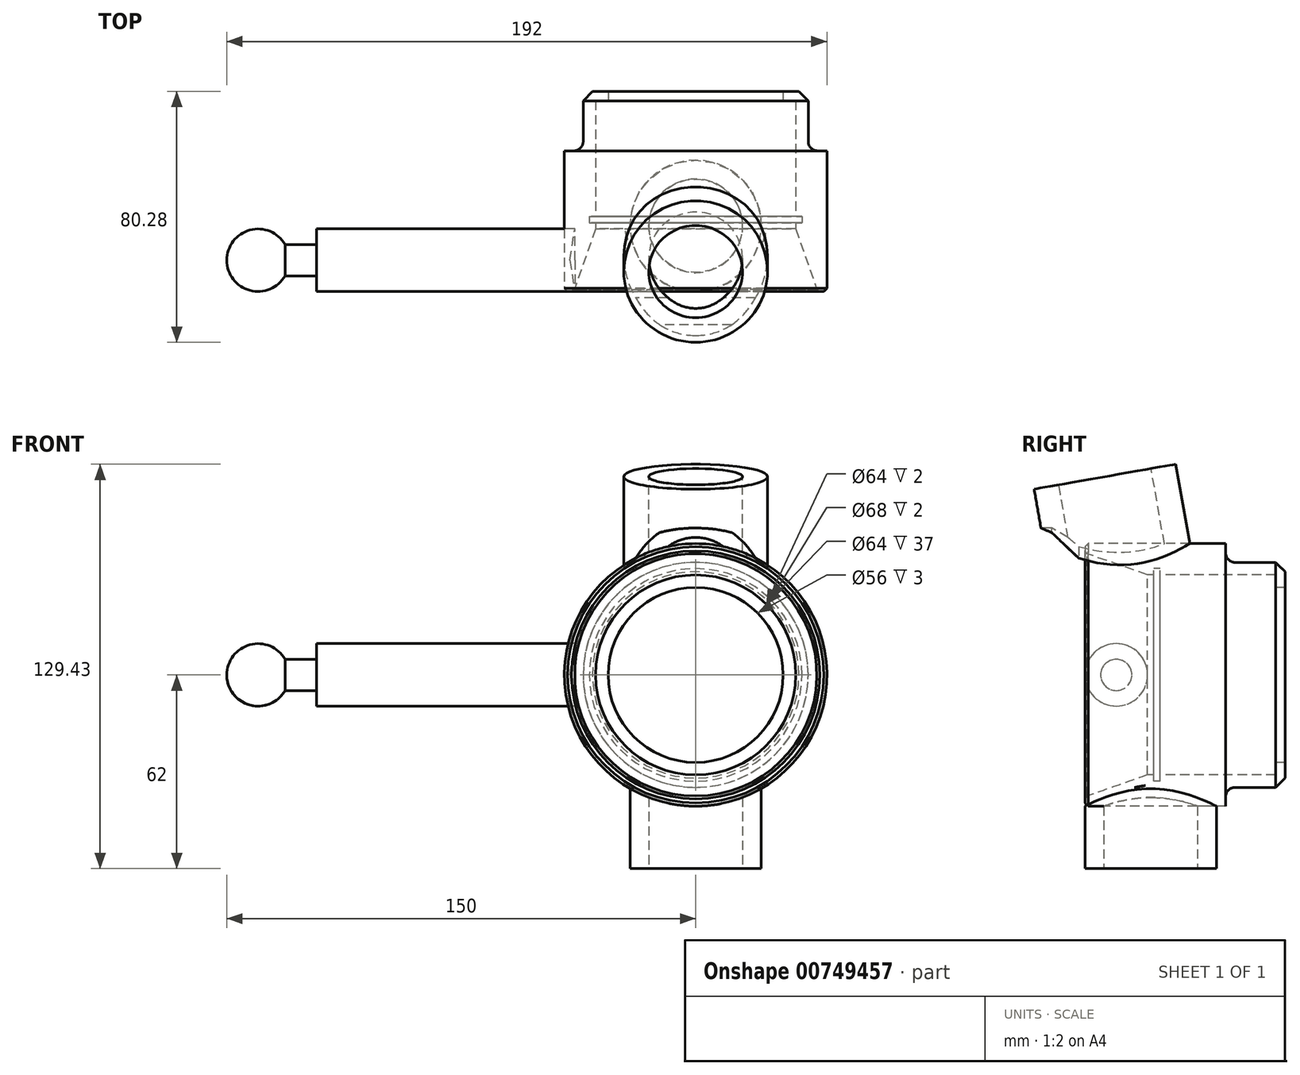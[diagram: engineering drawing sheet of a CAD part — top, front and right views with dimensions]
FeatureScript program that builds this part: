
annotation { "Feature Type Name" : "Feature", "Feature Type Description" : "" }
export const myFeature = defineFeature(function(context is Context, id is Id, definition is map)
    precondition{}
    {
        {
            var Q0;
            Q0=qCreatedBy(makeId("Right.planeOp"),FACE);
            var sketch = newSketch(context, id + "F0", { "sketchPlane" : qUnion([Q0])});
            skLineSegment(sketch, "E0", {"start": v(0, 42) * mm, "end": v(45, 42) * mm});
            skLineSegment(sketch, "E1", {"start": v(64, 36) * mm, "end": v(64, 28) * mm});
            skLineSegment(sketch, "E2", {"start": v(64, 28) * mm, "end": v(61, 28) * mm});
            skLineSegment(sketch, "E3", {"start": v(61, 28) * mm, "end": v(61, 32) * mm});
            skLineSegment(sketch, "E4", {"start": v(61, 32) * mm, "end": v(24, 32) * mm});
            skLineSegment(sketch, "E5", {"start": v(24, 32) * mm, "end": v(24, 34) * mm});
            skLineSegment(sketch, "E6", {"start": v(24, 34) * mm, "end": v(22, 34) * mm});
            skLineSegment(sketch, "E7", {"start": v(22, 34) * mm, "end": v(22, 32) * mm});
            skLineSegment(sketch, "E8", {"start": v(22, 32) * mm, "end": v(20, 32) * mm});
            skLineSegment(sketch, "E9", {"start": v(0, 39) * mm, "end": v(0, 42) * mm});
            skLineSegment(sketch, "E10", {"start": v(0, 0) * mm, "end": v(42.35, 0) * mm, "construction": true});
            skLineSegment(sketch, "E11", {"start": v(64, 36) * mm, "end": v(48, 36) * mm});
            skLineSegment(sketch, "E12", {"start": v(45, 39) * mm, "end": v(45, 42) * mm});
            skPoint(sketch, "E13.orphan", {"position": v(0, 32) * mm});
            skPoint(sketch, "E14.visualSharp", {"position": v(45, 36) * mm});
            skArc(sketch, "E14.filletArc", {"start": v(45, 39) * mm, "mid": v(45.88, 36.88) * mm, "end": v(48, 36) * mm});
            skPoint(sketch, "E15.visualSharp", {"position": v(19, 39) * mm});
            skLineSegment(sketch, "E16", {"start": v(0, 39) * mm, "end": v(20, 32) * mm});
            skSolve(sketch);
        }
        {
            var Q0;
            Q0 = qSketchRegion(id + "F0", true);
            var Q1;
            Q1=sQuery(id+"F0.wireOp",EDGE,"E10");
            revolve(context, id + "F1", {"surfaceOperationType" : NewSurfaceOperationType.NEW, "entities" : qUnion([Q0]), "axis" : qUnion([Q1]), "revolveType" : RevolveType.FULL});
        }
        {
            var Q0;
            Q0=qCreatedBy(makeId("Top.planeOp"),FACE);
            cPlane(context, id + "F2", {"entities" : qUnion([Q0]), "cplaneType" : CPlaneType.OFFSET, "offset" : (64 / 2 + 10) * mm, "oppositeDirection" : true, "width" : 150 * mm, "height" : 150 * mm});
        }
        {
            var Q0;
            Q0=qCreatedBy(id+"F2.planeOp",FACE);
            var sketch = newSketch(context, id + "F3", { "sketchPlane" : qUnion([Q0])});
            skCircle(sketch, "E17", {"center": v(0, 21) * mm, "radius": 21 * mm});
            skCircle(sketch, "E18", {"center": v(0, 21) * mm, "radius": 15 * mm});
            skSolve(sketch);
        }
        {
            var Q0;
            Q0 = qSketchRegion(id + "F3", true);
            extrude(context, id + "F4", {"entities" : qUnion([Q0]), "endBound" : BoundingType.UP_TO_NEXT, "depth" : 25 * mm, "offsetDistance" : 25 * mm, "hasSecondDirection" : true, "secondDirectionOppositeDirection" : true, "secondDirectionDepth" : 20 * mm});
        }
        {
            var Q0;
            Q0=qCreatedBy(makeId("Top.planeOp"),FACE);
            cPlane(context, id + "F5", {"entities" : qUnion([Q0]), "cplaneType" : CPlaneType.OFFSET, "offset" : (64 / 2 + 10) * mm, "width" : 150 * mm, "height" : 150 * mm});
        }
        {
            var Q0;
            Q0=qCreatedBy(id+"F5.planeOp",FACE);
            var sketch = newSketch(context, id + "F6", { "sketchPlane" : qUnion([Q0])});
            skLineSegment(sketch, "E19.0.0", {"start": v(42, 0) * mm, "end": v(-42, 0) * mm, "construction": true});
            skSolve(sketch);
        }
        {
            var Q0;
            Q0=sQuery(id+"F6.wireOp",EDGE,"E19.0.0");
            cPlane(context, id + "F7", {"entities" : qUnion([Q0]), "cplaneType" : CPlaneType.LINE_ANGLE, "offset" : 25 * mm, "angle" : 80 * degree, "width" : 150 * mm, "height" : 150 * mm});
        }
        {
            var Q0;
            Q0=qCreatedBy(id+"F7.planeOp",FACE);
            var sketch = newSketch(context, id + "F8", { "sketchPlane" : qUnion([Q0])});
            skCircle(sketch, "E20", {"center": v(0, 17.3) * mm, "radius": 23 * mm});
            skCircle(sketch, "E21", {"center": v(0, 17.3) * mm, "radius": 15 * mm});
            skSolve(sketch);
        }
        {
            var Q0;
            Q0=makeQuery(id+"F8.imprint","IMPRINT",FACE,{"disambiguationData":[TD([[makeQuery(id+"F8.imprint","IMPRINT",EDGE,{"derivedFrom":sQuery(id+"F8.wireOp",EDGE,"E20")}),1.0]])]});
            extrude(context, id + "F9", {"entities" : qUnion([Q0]), "oppositeDirection" : true, "depth" : 79.6 * mm, "offsetDistance" : 25 * mm, "hasSecondDirection" : true, "secondDirectionOppositeDirection" : false, "secondDirectionDepth" : 20 * mm});
        }
        {
            var Q0;
            Q0=qCreatedBy(makeId("Right.planeOp"),FACE);
            var sketch = newSketch(context, id + "F10", { "sketchPlane" : qUnion([Q0])});
            skLineSegment(sketch, "E22", {"start": v(45, 42) * mm, "end": v(-2, 42) * mm});
            skLineSegment(sketch, "E23", {"start": v(75.04, 0) * mm, "end": v(-49, 0) * mm});
            skLineSegment(sketch, "E24", {"start": v(-49, 0) * mm, "end": v(75.04, 0) * mm});
            skLineSegment(sketch, "E25", {"start": v(-49, 42) * mm, "end": v(-49, 0) * mm});
            skLineSegment(sketch, "E26.bottom", {"start": v(75.04, 42) * mm, "end": v(75.08, 42) * mm});
            skLineSegment(sketch, "E26.top", {"start": v(45, 62) * mm, "end": v(75.08, 62) * mm});
            skLineSegment(sketch, "E26.left", {"start": v(45, 42) * mm, "end": v(45, 62) * mm});
            skLineSegment(sketch, "E27", {"start": v(-2, 42) * mm, "end": v(-10.66, 47) * mm});
            skLineSegment(sketch, "E28", {"start": v(-10.66, 47) * mm, "end": v(-49, 47) * mm});
            skLineSegment(sketch, "E29", {"start": v(-49, 47) * mm, "end": v(-49, 42) * mm});
            skLineSegment(sketch, "E30", {"start": v(75.08, 62) * mm, "end": v(75.04, 0) * mm});
            skSolve(sketch);
        }
        {
            var Q0;
            Q0=makeQuery(id+"F10.imprint","IMPRINT",FACE,{"disambiguationData":[TD([[makeQuery(id+"F10.imprint","IMPRINT",EDGE,{"derivedFrom":sQuery(id+"F10.wireOp",EDGE,"E22")}),1.0]])]});
            var Q1;
            Q1=sQuery(id+"F10.wireOp",EDGE,"E24");
            revolve(context, id + "F11", {"surfaceOperationType" : NewSurfaceOperationType.NEW, "entities" : qUnion([Q0]), "axis" : qUnion([Q1]), "revolveType" : RevolveType.FULL});
        }
        {
            var Q0;
            Q0=makeQuery(id+"F1.opRevolve","SWEPT_EDGE",EDGE,{"disambiguationData":[OSD([sQuery(id+"F0.wireOp",EDGE,"E1"),sQuery(id+"F0.wireOp",EDGE,"E11")])]});
            chamfer(context, id + "F12", {"entities" : qUnion([Q0]), "width" : 3 * mm, "tangentPropagation" : true});
        }
        {
            var Q0;
            Q0=makeQuery(id+"F1.opRevolve","SWEPT_EDGE",EDGE,{"disambiguationData":[OSD([sQuery(id+"F0.wireOp",EDGE,"E9"),sQuery(id+"F0.wireOp",EDGE,"IUdjLPdn-Iqcu-OCA8-yRft-X54qKW0S89eC")])]});
            chamfer(context, id + "F13", {"entities" : qUnion([Q0]), "width" : 1 * mm, "tangentPropagation" : true});
        }
        {
            var Q0;
            Q0=makeQuery(id+"F11.opRevolve","SWEPT_BODY",BODY,{"disambiguationData":[OSD([sQuery(id+"F10.wireOp",EDGE,"E22"),sQuery(id+"F10.wireOp",EDGE,"E24"),sQuery(id+"F10.wireOp",EDGE,"E25"),sQuery(id+"F10.wireOp",EDGE,"E26.top"),sQuery(id+"F10.wireOp",EDGE,"E26.left"),sQuery(id+"F10.wireOp",EDGE,"E27"),sQuery(id+"F10.wireOp",EDGE,"E28"),sQuery(id+"F10.wireOp",EDGE,"E29"),sQuery(id+"F10.wireOp",EDGE,"E30")])]});
            var Q1;
            Q1=makeQuery(id+"F9.opExtrude","SWEPT_BODY",BODY,{"disambiguationData":[OSD([sQuery(id+"F8.wireOp",EDGE,"E20"),sQuery(id+"F8.wireOp",EDGE,"E21")])]});
            booleanBodies(context, id + "F14", {"operationType" : BooleanOperationType.SUBTRACTION, "tools" : qUnion([Q0]), "targets" : qUnion([Q1])});
        }
        {
            var Q0;
            Q0=makeQuery(id+"F1.opRevolve","SWEPT_FACE",FACE,{"disambiguationData":[OSD([sQuery(id+"F0.wireOp",EDGE,"E12")])]});
            cPlane(context, id + "F15", {"entities" : qUnion([Q0]), "cplaneType" : CPlaneType.OFFSET, "offset" : 35 * mm, "oppositeDirection" : true, "width" : 150 * mm, "height" : 150 * mm});
        }
        {
            var Q0;
            Q0=qCreatedBy(id+"F15.planeOp",FACE);
            var sketch = newSketch(context, id + "F16", { "sketchPlane" : qUnion([Q0])});
            skLineSegment(sketch, "E31", {"start": v(38.67, 10) * mm, "end": v(121.34, 10) * mm});
            skLineSegment(sketch, "E32", {"start": v(121.34, 10) * mm, "end": v(121.34, 5) * mm});
            skLineSegment(sketch, "E33", {"start": v(121.34, 5) * mm, "end": v(131.34, 5) * mm});
            skLineSegment(sketch, "E34", {"start": v(150, 0) * mm, "end": v(40.25, 0) * mm});
            skArc(sketch, "E35", {"start": v(131.34, 5) * mm, "mid": v(142.59, 9.66) * mm, "end": v(150, 0) * mm});
            skPoint(sketch, "E36.orphan", {"position": v(49.78, 10) * mm});
            skPoint(sketch, "E37.orphan", {"position": v(49.78, 0) * mm});
            skLineSegment(sketch, "E38", {"start": v(38.67, 10) * mm, "end": v(40.25, 0) * mm});
            skSolve(sketch);
        }
        {
            var Q0;
            Q0 = qSketchRegion(id + "F16", true);
            var Q1;
            Q1=sQuery(id+"F16.wireOp",EDGE,"E34");
            revolve(context, id + "F17", {"surfaceOperationType" : NewSurfaceOperationType.NEW, "entities" : qUnion([Q0]), "axis" : qUnion([Q1]), "revolveType" : RevolveType.FULL});
        }
    });
